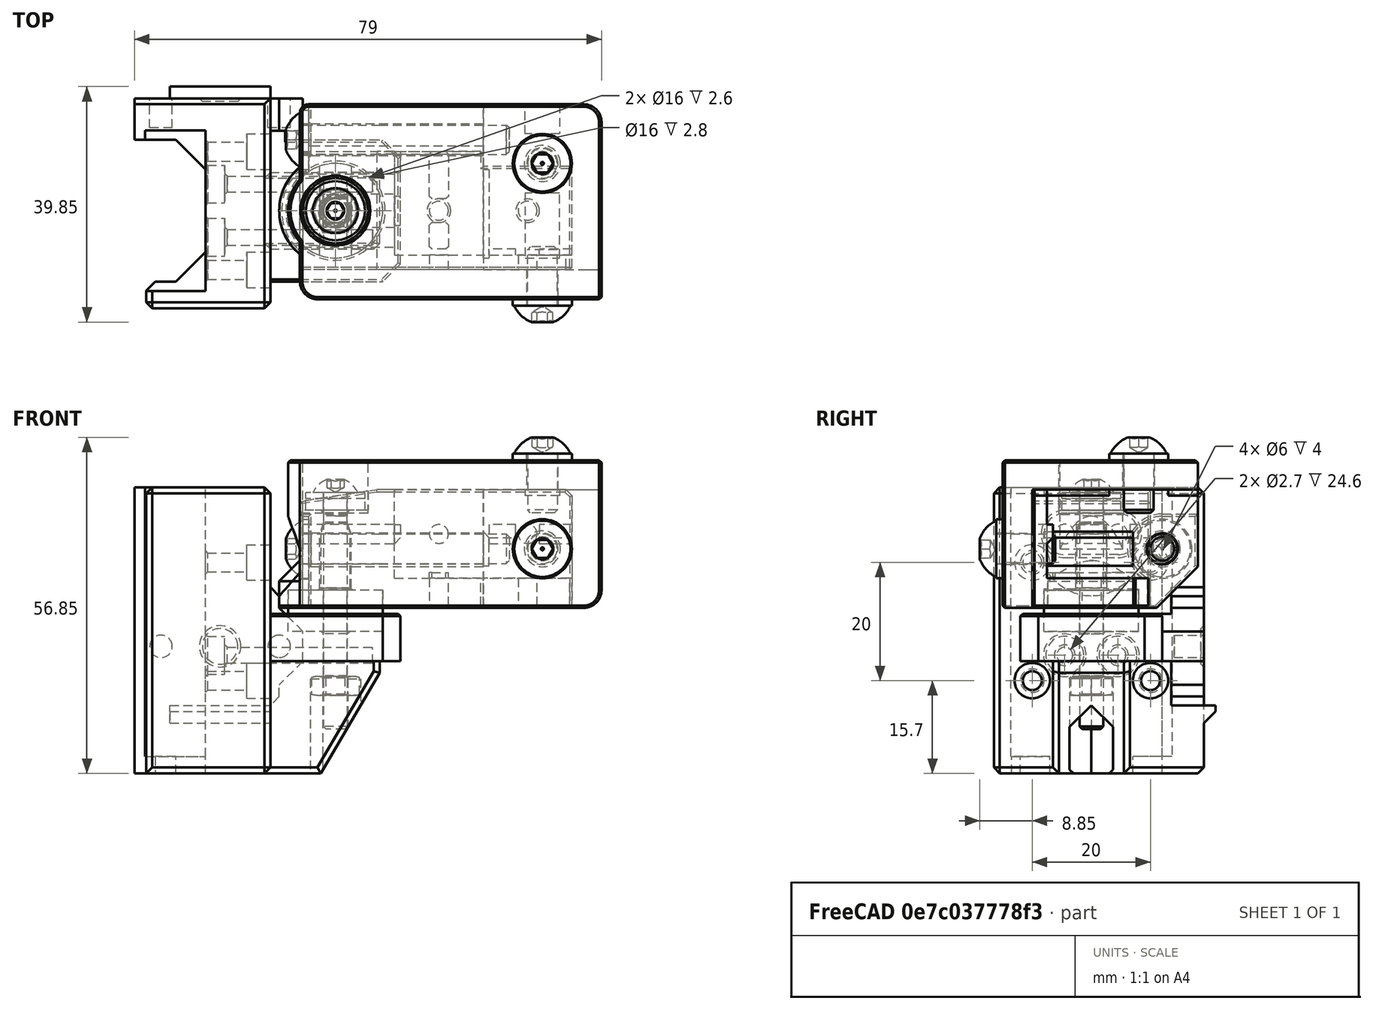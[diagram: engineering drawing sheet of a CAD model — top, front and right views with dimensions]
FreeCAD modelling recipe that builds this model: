
FCSTD DOCUMENT  (FreeCAD 0.19R24366 (Git))
Label: silicon-arm-assembly-tmp
License: All rights reserved
LicenseURL: http://en.wikipedia.org/wiki/All_rights_reserved
objects: Part::FeaturePython×16, Part::Feature×4, App::Part×2
note: 20 computed .brp shape members not serialized (recipe doc carries the construction recipe); baked Part::Feature solids carry a one-line shape summary decoded from their .brp

FEATURE [Part::Feature] Body001001  label="bed-arm001"
  Placement = pos=(32,0,25) rot=(0,0,1;0rad)
  shape: bbox 49.5 x 20 x 20 mm, 120 faces (baked)
FEATURE [Part::Feature] Body003001  label="rail-arm-fdm001"
  shape: bbox 45 x 37.5 x 48.4 mm, 126 faces (baked)
FEATURE [Part::FeaturePython] Tube  label="silicon-spacer-9mm-height"  # WARN: FeaturePython — macro-defined, semantics opaque (R4)
  AttacherType = Attacher::AttachEngine3D
  Height = 7
  InnerRadius = 2
  OuterRadius = 8
  Placement = pos=(22,0,21) rot=(0,0,1;0rad)
FEATURE [Part::FeaturePython] Nut  label="M4-Nut"  # Fasteners workbench fastener (typed FeaturePython)
  Placement = pos=(22,0,13.4) rot=(1,0,0;3.14159rad)
  baseObject = -> Body003001 [Edge1]
  diameter = 6
  invert = true
  leftHanded = false
  matchOuter = false
  offset = 0
  thread = false
  type = 11
FEATURE [Part::FeaturePython] Tube001  label="silicon-spacer-10x4x2"  # WARN: FeaturePython — macro-defined, semantics opaque (R4)
  AttacherType = Attacher::AttachEngine3D
  Height = 2
  InnerRadius = 2
  OuterRadius = 5
  Placement = pos=(22,0,41.5) rot=(0,0,1;0rad)
FEATURE [Part::FeaturePython] Tube002  label="m4x10x1-washer"  # WARN: FeaturePython — macro-defined, semantics opaque (R4)
  AttacherType = Attacher::AttachEngine3D
  Height = 1
  InnerRadius = 2
  OuterRadius = 5
  Placement = pos=(22,0,43.5) rot=(0,0,1;0rad)
FEATURE [Part::FeaturePython] Screw  label="M4x40-Screw"  # Fasteners workbench fastener (typed FeaturePython)
  Placement = pos=(22,0,44.5) rot=(0,0,1;0rad)
  baseObject = -> Tube002 [Edge4]
  diameter = 2
  invert = false
  leftHanded = false
  length = 10
  lengthCustom = 40
  matchOuter = false
  offset = 0
  thread = false
  type = 48
FEATURE [App::Part] Part  label="1515"
  Group = -> [Body001001,Body003001,Tube,Nut,Tube001,Tube002,Screw]
  Origin = -> Origin
FEATURE [Part::Feature] Body006002  label="rail-arm-fdm002"
  shape: bbox 45 x 37.5 x 48.4 mm, 126 faces (baked)
FEATURE [Part::FeaturePython] Tube003  label="silicon-spacer-9mm-height001"  # WARN: FeaturePython — macro-defined, semantics opaque (R4)
  AttacherType = Attacher::AttachEngine3D
  Height = 7
  InnerRadius = 2
  OuterRadius = 8
  Placement = pos=(22,0,21) rot=(0,0,1;0rad)
FEATURE [Part::FeaturePython] Nut001  label="M4-Nut001"  # Fasteners workbench fastener (typed FeaturePython)
  Placement = pos=(22,0,13.4) rot=(1,0,0;3.14159rad)
  baseObject = -> Body006002 [Edge1]
  diameter = 6
  invert = true
  leftHanded = false
  matchOuter = false
  offset = 0
  thread = false
  type = 11
FEATURE [Part::FeaturePython] Tube004  label="silicon-spacer-10x4x003"  # WARN: FeaturePython — macro-defined, semantics opaque (R4)
  AttacherType = Attacher::AttachEngine3D
  Height = 2
  InnerRadius = 2
  OuterRadius = 5
  Placement = pos=(22,0,41.5) rot=(0,0,1;0rad)
FEATURE [Part::FeaturePython] Tube005  label="m4x10x1-washer001"  # WARN: FeaturePython — macro-defined, semantics opaque (R4)
  AttacherType = Attacher::AttachEngine3D
  Height = 1
  InnerRadius = 2
  OuterRadius = 5
  Placement = pos=(22,0,43.5) rot=(0,0,1;0rad)
FEATURE [Part::FeaturePython] Screw001  label="M4x40-Screw001"  # Fasteners workbench fastener (typed FeaturePython)
  Placement = pos=(22,0,44.5) rot=(0,0,1;0rad)
  baseObject = -> Tube005 [Edge4]
  diameter = 2
  invert = false
  leftHanded = false
  length = 10
  lengthCustom = 40
  matchOuter = false
  offset = 0
  thread = false
  type = 48
FEATURE [Part::FeaturePython] Washer  label="M5-Washer"  # Fasteners workbench fastener (typed FeaturePython)
  Placement = pos=(57,-15,35) rot=(1,0,0;1.5708rad)
  diameter = 6
  invert = true
  matchOuter = false
  offset = 0
  type = 3
FEATURE [Part::FeaturePython] Screw002  label="M5x10-Screw"  # Fasteners workbench fastener (typed FeaturePython)
  Placement = pos=(57,-16.1,35) rot=(1,0,0;1.5708rad)
  baseObject = -> Washer [Edge1]
  diameter = 3
  invert = false
  leftHanded = false
  length = 1
  lengthCustom = 10
  matchOuter = false
  offset = 0
  thread = false
  type = 48
FEATURE [Part::FeaturePython] Washer001  label="M5-Washer003"  # Fasteners workbench fastener (typed FeaturePython)
  Placement = pos=(57,8,50) rot=(0,0,1;0rad)
  diameter = 6
  invert = true
  matchOuter = false
  offset = 0
  type = 3
FEATURE [Part::FeaturePython] Washer002  label="M5-Washer004"  # Fasteners workbench fastener (typed FeaturePython)
  Placement = pos=(17.5,12,35) rot=(0,-1,0;1.5708rad)
  diameter = 6
  invert = false
  matchOuter = false
  offset = 0
  type = 3
FEATURE [Part::FeaturePython] Screw003  label="M5x10-Screw001"  # Fasteners workbench fastener (typed FeaturePython)
  Placement = pos=(57,8,51.1) rot=(0,0,1;0rad)
  baseObject = -> Washer001 [Edge1]
  diameter = 3
  invert = false
  leftHanded = false
  length = 1
  lengthCustom = 10
  matchOuter = false
  offset = 0
  thread = false
  type = 48
FEATURE [Part::FeaturePython] Screw004  label="M5x35-Screw"  # Fasteners workbench fastener (typed FeaturePython)
  Placement = pos=(16.4,12,35) rot=(0,-1,0;1.5708rad)
  baseObject = -> Washer002 [Edge1]
  diameter = 3
  invert = false
  leftHanded = false
  length = 8
  lengthCustom = 35
  matchOuter = false
  offset = 0
  thread = false
  type = 48
FEATURE [Part::Feature] Chamfer004013007011015006009007001005003063003001002001002001007002027001
  Placement = pos=(22,0,25) rot=(0,0,1;0rad)
  shape: bbox 54.5 x 33 x 25 mm, 94 faces (baked)
FEATURE [App::Part] Part001  label="2020"
  Group = -> [Body006002,Tube003,Nut001,Tube004,Tube005,Screw001,Washer,Screw002,Washer001,Washer002,Screw003,Screw004,Chamfer004013007011015006009007001005003063003001002001002001007002027001]
  Origin = -> Origin001
